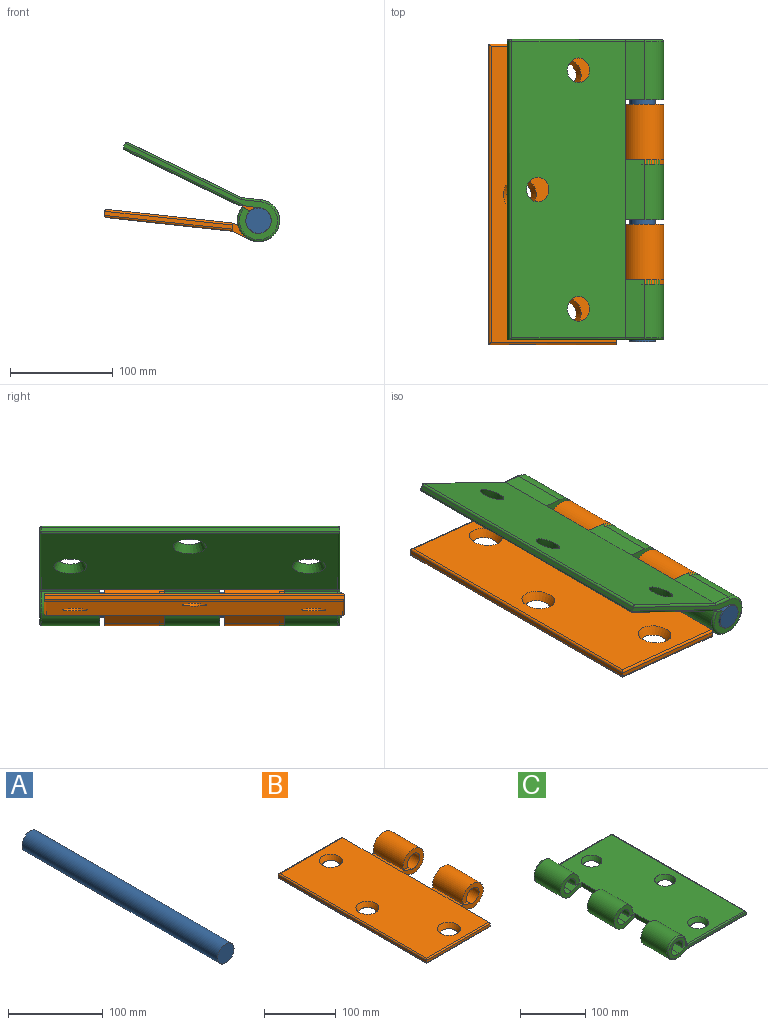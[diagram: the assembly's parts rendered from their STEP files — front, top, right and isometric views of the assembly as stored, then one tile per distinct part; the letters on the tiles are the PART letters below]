
ASSEMBLY  parts=3 mates=2
PART A: 3 faces, bbox 24.5x292x24.5 mm
  f0: cylinder r=12.25mm len=292mm, axis (0,-1,0), area 22475mm2, adj f1,f2
  f1: plane 24.5x24.5mm, normal (0,1,0), area 471.4mm2, adj f0
  f2: plane 24.5x24.5mm, normal (0,-1,0), area 471.4mm2, adj f0
PART B: 31 faces, bbox 170x292x41 mm
  f0: plane 58.4x20.54mm, normal (0.32,0,0.95), area 1264.7mm2, adj f8,f12,f22,f24
  f1: plane 58.4x20.54mm, normal (0.32,0,0.95), area 1264.7mm2, adj f9,f12,f19,f21
  f2: plane 58.4x17.59mm, normal (-0.34,0,-0.94), area 1091mm2, adj f4,f14,f22,f24
  f3: plane 58.4x17.59mm, normal (-0.34,0,-0.94), area 1091mm2, adj f5,f14,f19,f21
  f4: cylinder r=20.5mm len=58.4mm, axis (0,1,0), area 6348.4mm2, adj f2,f6,f22,f24
  f5: cylinder r=20.5mm len=58.4mm, axis (0,1,0), area 6348.4mm2, adj f3,f7,f19,f21
  f6: plane 58.4x8.42mm, normal (0,0,-1), area 492mm2, adj f4,f8,f22,f24
  f7: plane 58.4x8.42mm, normal (0,0,-1), area 492mm2, adj f5,f9,f19,f21
  f8: cylinder r=12.5mm len=58.4mm, axis (0,1,0), area 3975.6mm2, adj f0,f6,f22,f24
  f9: cylinder r=12.5mm len=58.4mm, axis (0,1,0), area 3975.6mm2, adj f1,f7,f19,f21
  f10: plane 125x4mm, normal (0,-1,0), area 500mm2, adj f13,f23,f25,f28
  f11: plane 125x4mm, normal (0,1,0), area 500mm2, adj f13,f18,f26,f29
  f12: plane 288x123mm, normal (0,0,1), area 33011.3mm2, adj f0,f1,f15,f16,f17,f18,f20,f23
  f13: plane 292x4mm, normal (-1,0,0), area 1168mm2, adj f10,f11,f27,f30
  f14: plane 288x123mm, normal (0,0,-1), area 34066.8mm2, adj f2,f3,f15,f16,f17,f18,f20,f23
  f15: cone r=12mm half-angle=26.6deg, axis (0,0,1), area 786.8mm2, adj f12,f14
  f16: cone r=12mm half-angle=26.6deg, axis (0,0,1), area 786.8mm2, adj f12,f14
  f17: cone r=12mm half-angle=26.6deg, axis (0,0,1), area 786.8mm2, adj f12,f14
  f18: plane 58.4x8mm, normal (1,0,0), area 465.5mm2, adj f11,f12,f14,f19,f26,f29
  f19: plane 45x41mm, normal (0,1,0), area 864mm2, adj f1,f3,f5,f7,f9,f18
  f20: plane 58.4x8mm, normal (1,0,0), area 467.2mm2, adj f12,f14,f21,f22
  f21: plane 45x41mm, normal (0,-1,0), area 864mm2, adj f1,f3,f5,f7,f9,f20
  f22: plane 45x41mm, normal (0,1,0), area 864mm2, adj f0,f2,f4,f6,f8,f20
  f23: plane 58.4x8mm, normal (1,0,0), area 465.5mm2, adj f10,f12,f14,f24,f25,f28
  f24: plane 45x41mm, normal (0,-1,0), area 864mm2, adj f0,f2,f4,f6,f8,f23
  f25: cylinder r=2mm len=125mm, axis (1,0,0), area 390.4mm2, adj f10,f12,f23,f27
  f26: cylinder r=2mm len=125mm, axis (-1,0,0), area 390.4mm2, adj f11,f12,f18,f27
  f27: cylinder r=2mm len=292mm, axis (0,1,0), area 912.8mm2, adj f12,f13,f25,f26
  f28: cylinder r=2mm len=125mm, axis (-1,0,0), area 390.4mm2, adj f10,f14,f23,f30
  f29: cylinder r=2mm len=125mm, axis (1,0,0), area 390.4mm2, adj f11,f14,f18,f30
  f30: cylinder r=2mm len=292mm, axis (0,1,0), area 912.8mm2, adj f13,f14,f28,f29
PART C: 42 faces, bbox 171.7x292x44.4 mm
  f0: plane 58.4x20.54mm, normal (-0.32,0,0.95), area 1264.7mm2, adj f8,f11,f25,f27
  f1: plane 58.4x20.54mm, normal (-0.32,0,0.95), area 1262mm2, adj f9,f11,f18,f24,f30
  f2: plane 58.4x17.59mm, normal (0.34,0,-0.94), area 1091mm2, adj f4,f13,f25,f27
  f3: plane 56.4x17.59mm, normal (0.34,0,-0.94), area 1053.6mm2, adj f5,f13,f24,f36
  f4: cylinder r=20.5mm len=58.4mm, axis (0,1,0), area 6348.4mm2, adj f2,f6,f25,f27
  f5: cylinder r=20.5mm len=56.4mm, axis (0,1,0), area 6131mm2, adj f3,f7,f24,f35
  f6: plane 58.4x8.42mm, normal (0,0,-1), area 492mm2, adj f4,f8,f25,f27
  f7: plane 58.4x8.42mm, normal (0,0,-1), area 491.1mm2, adj f5,f9,f18,f24,f35
  f8: cylinder r=12.5mm len=58.4mm, axis (0,1,0), area 3975.6mm2, adj f0,f6,f25,f27
  f9: cylinder r=12.5mm len=58.4mm, axis (0,1,0), area 3975.6mm2, adj f1,f7,f18,f24
  f10: plane 58.4x20.54mm, normal (-0.32,0,0.95), area 1262mm2, adj f11,f17,f19,f28,f37
  f11: plane 288x123mm, normal (0,0,1), area 33011.3mm2, adj f0,f1,f10,f20,f21,f22,f23,f26
  f12: plane 290x4mm, normal (1,0,0), area 1160mm2, adj f18,f29,f31,f41
  f13: plane 288x123mm, normal (0,0,-1), area 34066.8mm2, adj f2,f3,f14,f20,f21,f22,f23,f26
  f14: plane 56.4x17.59mm, normal (0.34,0,-0.94), area 1053.6mm2, adj f13,f15,f28,f34
  f15: cylinder r=20.5mm len=56.4mm, axis (0,1,0), area 6131mm2, adj f14,f16,f28,f33
  f16: plane 58.4x8.42mm, normal (0,0,-1), area 491.1mm2, adj f15,f17,f19,f28,f33
  f17: cylinder r=12.5mm len=58.4mm, axis (0,1,0), area 3975.6mm2, adj f10,f16,f19,f28
  f18: plane 168x37mm, normal (0,-1,0), area 1112.6mm2, adj f1,f7,f9,f12,f30,f32,f35,f36
  f19: plane 166x37mm, normal (0,1,0), area 1104.6mm2, adj f10,f16,f17,f33,f34,f37,f38,f41
  f20: cone r=12mm half-angle=26.6deg, axis (0,0,1), area 786.8mm2, adj f11,f13
  f21: cone r=12mm half-angle=26.6deg, axis (0,0,1), area 786.8mm2, adj f11,f13
  f22: cone r=12mm half-angle=26.6deg, axis (0,0,1), area 786.8mm2, adj f11,f13
  f23: plane 58.4x8mm, normal (-1,0,0), area 467.2mm2, adj f11,f13,f24,f25
  f24: plane 45x41mm, normal (0,1,0), area 864mm2, adj f1,f3,f5,f7,f9,f23
  f25: plane 45x41mm, normal (0,-1,0), area 864mm2, adj f0,f2,f4,f6,f8,f23
  f26: plane 58.4x8mm, normal (-1,0,0), area 467.2mm2, adj f11,f13,f27,f28
  f27: plane 45x41mm, normal (0,1,0), area 864mm2, adj f0,f2,f4,f6,f8,f26
  f28: plane 45x41mm, normal (0,-1,0), area 864mm2, adj f10,f14,f15,f16,f17,f26
  f29: cylinder r=2mm len=290mm, axis (0,1,0), area 908.8mm2, adj f11,f12,f30,f39
  f30: cylinder r=2mm len=130.99mm, axis (-1,0,0), area 397.3mm2, adj f1,f11,f18,f29
  f31: cylinder r=2mm len=290mm, axis (0,1,0), area 908.8mm2, adj f12,f13,f32,f40
  f32: cylinder r=2mm len=125.35mm, axis (1,0,0), area 390.8mm2, adj f13,f18,f31,f36
  f33: torus R=18.5mm, axis (0,-1,0), area 330mm2, adj f15,f16,f19,f34
  f34: cylinder r=2mm len=18.59mm, axis (-0.94,0,-0.34), area 59.1mm2, adj f14,f19,f33,f38
  f35: torus R=18.5mm, axis (0,-1,0), area 330mm2, adj f5,f7,f18,f36
  f36: cylinder r=2mm len=18.59mm, axis (0.94,0,0.34), area 59.1mm2, adj f3,f18,f32,f35
  f37: cylinder r=2mm len=128.99mm, axis (1,0,0), area 393.3mm2, adj f10,f11,f19,f39
  f38: cylinder r=2mm len=123.35mm, axis (-1,0,0), area 386.8mm2, adj f13,f19,f34,f40
  f39: sphere r=2mm, area 6.3mm2, adj f29,f37,f41
  f40: sphere r=2mm, area 6.3mm2, adj f31,f38,f41
  f41: cylinder r=2mm len=4mm, axis (0,0,-1), area 12.6mm2, adj f12,f19,f39,f40
PLACE A at identity fixed
PLACE B rot(axis=(0,1,0),6.2deg) t=(-0.4,-2.86,2.66)mm
PLACE C rot(axis=(0,-1,0),154.2deg) t=(48.73,1.71,-1.17)mm
MATE cylindrical C.f4 <-> A.f0  axis (0,1,0) through (24.5,-144.29,5)mm
MATE cylindrical B.f4 <-> A.f0  axis (0,1,0) through (24.5,-178.06,5)mm
